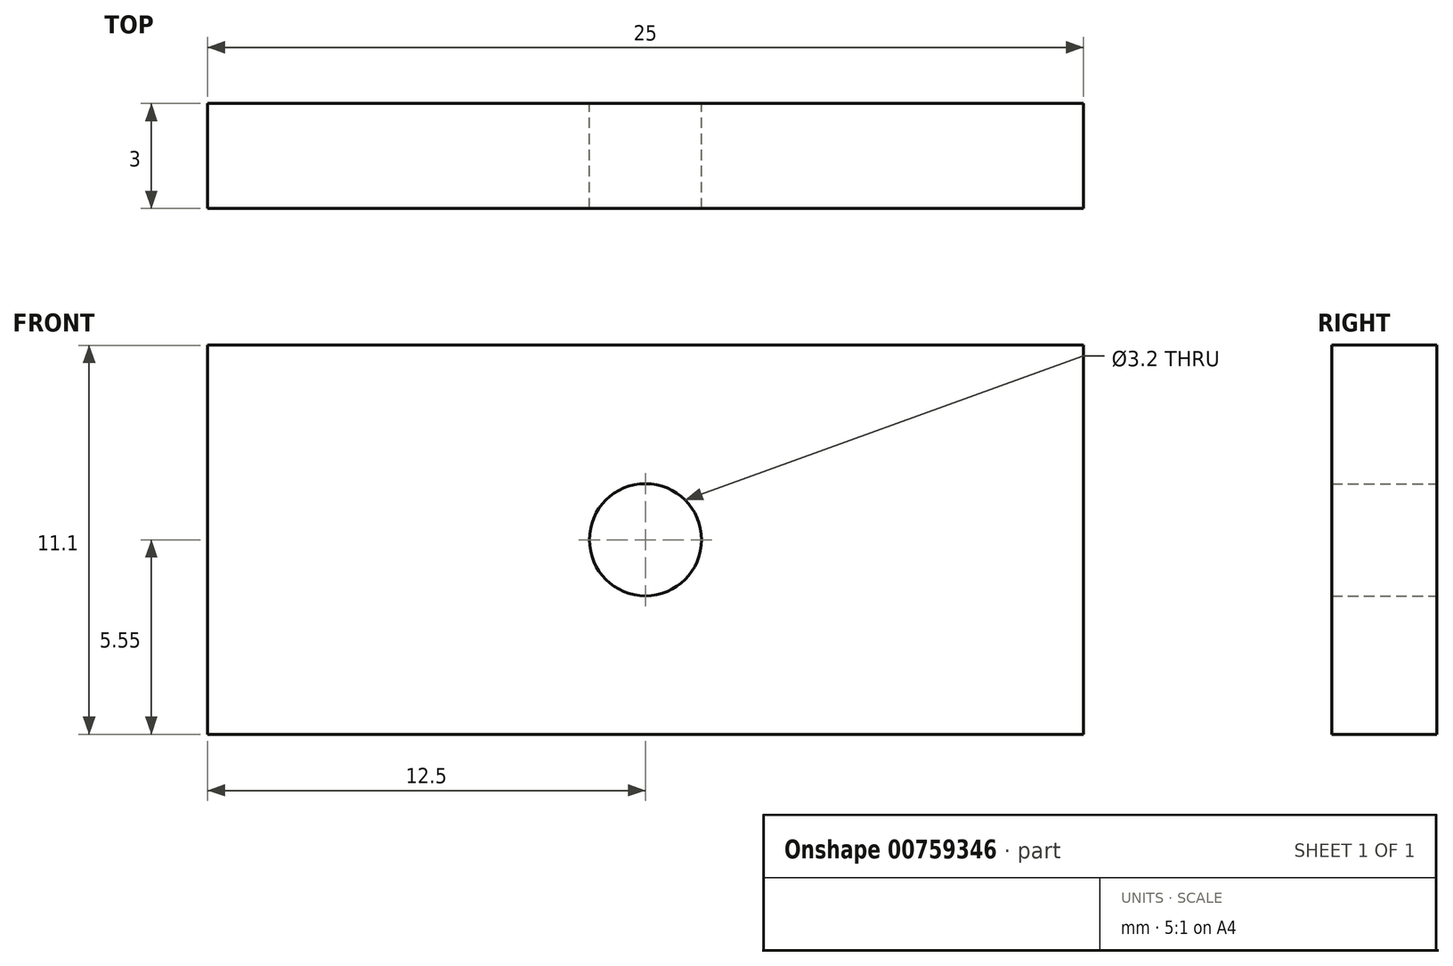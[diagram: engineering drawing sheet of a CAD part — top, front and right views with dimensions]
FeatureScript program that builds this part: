
annotation { "Feature Type Name" : "Feature", "Feature Type Description" : "" }
export const myFeature = defineFeature(function(context is Context, id is Id, definition is map)
    precondition{}
    {
        {
            var Q0;
            Q0=qCreatedBy(makeId("Front.planeOp"),FACE);
            var sketch = newSketch(context, id + "F0", { "sketchPlane" : qUnion([Q0])});
            skLineSegment(sketch, "E0.bottom", {"start": v(12.5, 5.56) * mm, "end": v(-12.5, 5.56) * mm});
            skLineSegment(sketch, "E0.top", {"start": v(12.5, -5.55) * mm, "end": v(-12.5, -5.55) * mm});
            skLineSegment(sketch, "E0.left", {"start": v(12.5, 5.56) * mm, "end": v(12.5, -5.55) * mm});
            skLineSegment(sketch, "E0.right", {"start": v(-12.5, 5.56) * mm, "end": v(-12.5, -5.55) * mm});
            skPoint(sketch, "E0.middle", {"position": v(0, 0) * mm});
            skCircle(sketch, "E1", {"center": v(0, 0) * mm, "radius": 1.6 * mm});
            skSolve(sketch);
        }
        {
            var Q0;
            Q0=makeQuery(id+"F0.imprint","IMPRINT",FACE,{"disambiguationData":[TD([[makeQuery(id+"F0.imprint","IMPRINT",EDGE,{"derivedFrom":sQuery(id+"F0.wireOp",EDGE,"E0.bottom")}),1.0]])]});
            extrude(context, id + "F1", {"entities" : qUnion([Q0]), "depth" : 3 * mm, "offsetDistance" : 25 * mm});
        }
    });
